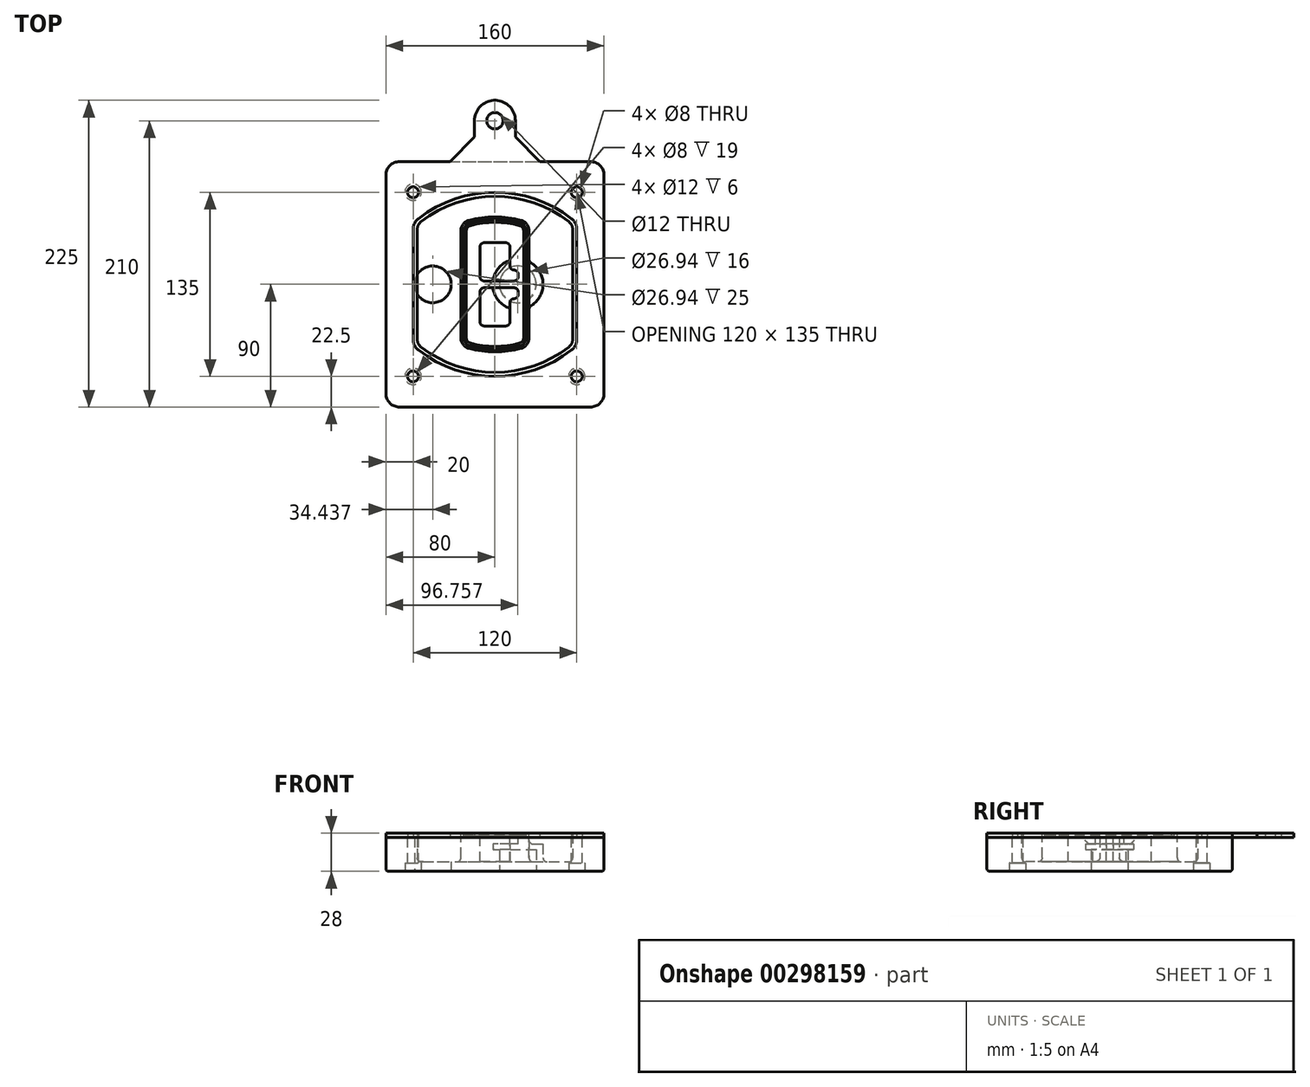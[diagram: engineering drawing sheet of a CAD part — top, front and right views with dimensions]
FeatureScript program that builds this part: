
annotation { "Feature Type Name" : "Feature", "Feature Type Description" : "" }
export const myFeature = defineFeature(function(context is Context, id is Id, definition is map)
    precondition{}
    {
        {
            var Q0;
            Q0=qCreatedBy(makeId("Top.planeOp"),FACE);
            var sketch = newSketch(context, id + "F0", { "sketchPlane" : qUnion([Q0])});
            skPoint(sketch, "E0.rect.middle", {"position": v(0, 0) * mm});
            skLineSegment(sketch, "E1.bottom", {"start": v(-70, -90) * mm, "end": v(70, -90) * mm});
            skLineSegment(sketch, "E1.top", {"start": v(-70, 90) * mm, "end": v(70, 90) * mm});
            skLineSegment(sketch, "E1.left", {"start": v(-80, -80) * mm, "end": v(-80, 80) * mm});
            skLineSegment(sketch, "E1.right", {"start": v(80, -80) * mm, "end": v(80, 80) * mm});
            skLineSegment(sketch, "E2", {"start": v(-80, 90) * mm, "end": v(80, -90) * mm, "construction": true});
            skLineSegment(sketch, "E3", {"start": v(80, 90) * mm, "end": v(-80, -90) * mm, "construction": true});
            skCircle(sketch, "E4", {"center": v(-60, 67.5) * mm, "radius": 4 * mm});
            skCircle(sketch, "E5", {"center": v(60, 67.5) * mm, "radius": 4 * mm});
            skCircle(sketch, "E6", {"center": v(60, -67.5) * mm, "radius": 4 * mm});
            skCircle(sketch, "E7", {"center": v(-60, -67.5) * mm, "radius": 4 * mm});
            skLineSegment(sketch, "E8", {"start": v(-60, 67.5) * mm, "end": v(60, 67.5) * mm, "construction": true});
            skLineSegment(sketch, "E9", {"start": v(60, 67.5) * mm, "end": v(60, -67.5) * mm, "construction": true});
            skLineSegment(sketch, "E10", {"start": v(60, -67.5) * mm, "end": v(-60, -67.5) * mm, "construction": true});
            skLineSegment(sketch, "E11", {"start": v(-60, -67.5) * mm, "end": v(-60, 67.5) * mm, "construction": true});
            skLineSegment(sketch, "E12", {"start": v(-60, 40.3) * mm, "end": v(-60, -40.3) * mm});
            skLineSegment(sketch, "E13", {"start": v(60, 40.3) * mm, "end": v(60, -40.3) * mm});
            skArc(sketch, "E14", {"start": v(56.15, 48.18) * mm, "mid": v(0, 67.5) * mm, "end": v(-56.15, 48.18) * mm});
            skArc(sketch, "E15", {"start": v(-56.15, -48.18) * mm, "mid": v(0, -67.5) * mm, "end": v(56.15, -48.18) * mm});
            skLineSegment(sketch, "E16", {"start": v(-60, 0) * mm, "end": v(60, 0) * mm, "construction": true});
            skPoint(sketch, "E17.visualSharp", {"position": v(-60, -45) * mm});
            skArc(sketch, "E17.filletArc", {"start": v(-60, -40.3) * mm, "mid": v(-58.99, -44.68) * mm, "end": v(-56.15, -48.18) * mm});
            skPoint(sketch, "E18.visualSharp", {"position": v(-60, 45) * mm});
            skArc(sketch, "E18.filletArc", {"start": v(-56.15, 48.18) * mm, "mid": v(-58.99, 44.68) * mm, "end": v(-60, 40.3) * mm});
            skPoint(sketch, "E19.visualSharp", {"position": v(60, 45) * mm});
            skArc(sketch, "E19.filletArc", {"start": v(60, 40.3) * mm, "mid": v(58.99, 44.68) * mm, "end": v(56.15, 48.18) * mm});
            skPoint(sketch, "E20.visualSharp", {"position": v(60, -45) * mm});
            skArc(sketch, "E20.filletArc", {"start": v(56.15, -48.18) * mm, "mid": v(58.99, -44.68) * mm, "end": v(60, -40.3) * mm});
            skPoint(sketch, "E21.visualSharp", {"position": v(-80, 90) * mm});
            skArc(sketch, "E21.filletArc", {"start": v(-70, 90) * mm, "mid": v(-77.07, 87.07) * mm, "end": v(-80, 80) * mm});
            skPoint(sketch, "E22.visualSharp", {"position": v(80, 90) * mm});
            skArc(sketch, "E22.filletArc", {"start": v(80, 80) * mm, "mid": v(77.07, 87.07) * mm, "end": v(70, 90) * mm});
            skPoint(sketch, "E23.visualSharp", {"position": v(80, -90) * mm});
            skArc(sketch, "E23.filletArc", {"start": v(70, -90) * mm, "mid": v(77.07, -87.07) * mm, "end": v(80, -80) * mm});
            skPoint(sketch, "E24.visualSharp", {"position": v(-80, -90) * mm});
            skArc(sketch, "E24.filletArc", {"start": v(-80, -80) * mm, "mid": v(-77.07, -87.07) * mm, "end": v(-70, -90) * mm});
            skArc(sketch, "E25.0", {"start": v(57, 40.3) * mm, "mid": v(56.3, 43.36) * mm, "end": v(54.3, 45.81) * mm});
            skLineSegment(sketch, "E25.1", {"start": v(57, 40.3) * mm, "end": v(57, -40.3) * mm});
            skArc(sketch, "E25.2", {"start": v(54.3, -45.81) * mm, "mid": v(56.3, -43.36) * mm, "end": v(57, -40.3) * mm});
            skArc(sketch, "E25.3", {"start": v(-54.3, -45.81) * mm, "mid": v(0, -64.5) * mm, "end": v(54.3, -45.81) * mm});
            skArc(sketch, "E25.4", {"start": v(-57, -40.3) * mm, "mid": v(-56.3, -43.36) * mm, "end": v(-54.3, -45.81) * mm});
            skArc(sketch, "E25.5", {"start": v(54.3, 45.81) * mm, "mid": v(0, 64.5) * mm, "end": v(-54.3, 45.81) * mm});
            skLineSegment(sketch, "E25.6", {"start": v(-57, 40.3) * mm, "end": v(-57, -40.3) * mm});
            skArc(sketch, "E25.7", {"start": v(-54.3, 45.81) * mm, "mid": v(-56.3, 43.36) * mm, "end": v(-57, 40.3) * mm});
            skArc(sketch, "E26.0", {"start": v(-58.62, 51.33) * mm, "mid": v(-62.58, 46.43) * mm, "end": v(-64, 40.3) * mm});
            skArc(sketch, "E26.1", {"start": v(58.62, 51.33) * mm, "mid": v(0, 71.5) * mm, "end": v(-58.62, 51.33) * mm});
            skArc(sketch, "E26.2", {"start": v(64, 40.3) * mm, "mid": v(62.58, 46.43) * mm, "end": v(58.62, 51.33) * mm});
            skLineSegment(sketch, "E26.3", {"start": v(64, 40.3) * mm, "end": v(64, -40.3) * mm});
            skArc(sketch, "E26.4", {"start": v(58.62, -51.33) * mm, "mid": v(62.58, -46.43) * mm, "end": v(64, -40.3) * mm});
            skLineSegment(sketch, "E26.5", {"start": v(-64, 40.3) * mm, "end": v(-64, -40.3) * mm});
            skArc(sketch, "E26.6", {"start": v(-58.62, -51.33) * mm, "mid": v(0, -71.5) * mm, "end": v(58.62, -51.33) * mm});
            skArc(sketch, "E26.7", {"start": v(-64, -40.3) * mm, "mid": v(-62.58, -46.43) * mm, "end": v(-58.62, -51.33) * mm});
            skSolve(sketch);
        }
        {
            var Q0;
            Q0=makeQuery(id+"F0.imprint","IMPRINT",FACE,{"disambiguationData":[TD([[makeQuery(id+"F0.imprint","IMPRINT",EDGE,{"derivedFrom":sQuery(id+"F0.wireOp",EDGE,"E1.bottom")}),1.0]])]});
            var Q1;
            Q1=makeQuery(id+"F0.imprint","IMPRINT",FACE,{"disambiguationData":[TD([[makeQuery(id+"F0.imprint","IMPRINT",EDGE,{"derivedFrom":sQuery(id+"F0.wireOp",EDGE,"E12")}),1.0]])]});
            var Q2;
            Q2=makeQuery(id+"F0.imprint","IMPRINT",FACE,{"disambiguationData":[TD([[makeQuery(id+"F0.imprint","IMPRINT",EDGE,{"derivedFrom":sQuery(id+"F0.wireOp",EDGE,"E25.0")}),1.0]])]});
            var Q3;
            Q3=makeQuery(id+"F0.imprint","IMPRINT",FACE,{"disambiguationData":[TD([[makeQuery(id+"F0.imprint","IMPRINT",EDGE,{"derivedFrom":sQuery(id+"F0.wireOp",EDGE,"E12")}),-1.0]])]});
            extrude(context, id + "F1", {"entities" : qUnion([Q0, Q1, Q2, Q3]), "oppositeDirection" : true, "depth" : 25 * mm});
        }
        {
            var Q0;
            Q0=makeQuery(id+"F0.imprint","IMPRINT",FACE,{"disambiguationData":[TD([[makeQuery(id+"F0.imprint","IMPRINT",EDGE,{"derivedFrom":sQuery(id+"F0.wireOp",EDGE,"E12")}),1.0]])]});
            extrude(context, id + "F2", {"entities" : qUnion([Q0]), "operationType" : NewBodyOperationType.ADD, "depth" : 3 * mm});
        }
        {
            var Q0;
            Q0=makeQuery(id+"F0.imprint","IMPRINT",FACE,{"disambiguationData":[TD([[makeQuery(id+"F0.imprint","IMPRINT",EDGE,{"derivedFrom":sQuery(id+"F0.wireOp",EDGE,"E25.0")}),1.0]])]});
            extrude(context, id + "F3", {"entities" : qUnion([Q0]), "operationType" : NewBodyOperationType.REMOVE, "oppositeDirection" : true, "depth" : 18 * mm});
        }
        {
            var Q0;
            Q0=makeQuery(id+"F2.opExtrude","CAP_FACE",FACE,{"disambiguationData":[OSD([sQuery(id+"F0.wireOp",EDGE,"E12"),sQuery(id+"F0.wireOp",EDGE,"E13"),sQuery(id+"F0.wireOp",EDGE,"E14"),sQuery(id+"F0.wireOp",EDGE,"E15"),sQuery(id+"F0.wireOp",EDGE,"E17.filletArc"),sQuery(id+"F0.wireOp",EDGE,"E18.filletArc"),sQuery(id+"F0.wireOp",EDGE,"E19.filletArc"),sQuery(id+"F0.wireOp",EDGE,"E20.filletArc"),sQuery(id+"F0.wireOp",EDGE,"E25.0"),sQuery(id+"F0.wireOp",EDGE,"E25.1"),sQuery(id+"F0.wireOp",EDGE,"E25.2"),sQuery(id+"F0.wireOp",EDGE,"E25.3"),sQuery(id+"F0.wireOp",EDGE,"E25.4"),sQuery(id+"F0.wireOp",EDGE,"E25.5"),sQuery(id+"F0.wireOp",EDGE,"E25.6"),sQuery(id+"F0.wireOp",EDGE,"E25.7")])],"isStart":false});
            var sketch = newSketch(context, id + "F4", { "sketchPlane" : qUnion([Q0])});
            skArc(sketch, "E27.0", {"start": v(-19.08, -46.97) * mm, "mid": v(0, -49.5) * mm, "end": v(19.08, -46.97) * mm});
            skArc(sketch, "E28.0", {"start": v(19.08, 46.97) * mm, "mid": v(0, 49.5) * mm, "end": v(-19.08, 46.97) * mm});
            skLineSegment(sketch, "E29", {"start": v(-25, 39.25) * mm, "end": v(-25, -39.25) * mm});
            skLineSegment(sketch, "E30", {"start": v(25, 39.25) * mm, "end": v(25, -39.25) * mm});
            skLineSegment(sketch, "E31", {"start": v(-25, 45.1) * mm, "end": v(25, 45.1) * mm, "construction": true});
            skLineSegment(sketch, "E32", {"start": v(-25, -45.1) * mm, "end": v(25, -45.1) * mm, "construction": true});
            skPoint(sketch, "E33.visualSharp", {"position": v(-25, 45.1) * mm});
            skArc(sketch, "E33.filletArc", {"start": v(-19.08, 46.97) * mm, "mid": v(-23.35, 44.11) * mm, "end": v(-25, 39.25) * mm});
            skPoint(sketch, "E34.visualSharp", {"position": v(25, 45.1) * mm});
            skArc(sketch, "E34.filletArc", {"start": v(25, 39.25) * mm, "mid": v(23.35, 44.11) * mm, "end": v(19.08, 46.97) * mm});
            skPoint(sketch, "E35.visualSharp", {"position": v(25, -45.1) * mm});
            skArc(sketch, "E35.filletArc", {"start": v(19.08, -46.97) * mm, "mid": v(23.35, -44.11) * mm, "end": v(25, -39.25) * mm});
            skPoint(sketch, "E36.visualSharp", {"position": v(-25, -45.1) * mm});
            skArc(sketch, "E36.filletArc", {"start": v(-25, -39.25) * mm, "mid": v(-23.35, -44.11) * mm, "end": v(-19.08, -46.97) * mm});
            skArc(sketch, "E37.0", {"start": v(54.3, 45.81) * mm, "mid": v(0, 64.5) * mm, "end": v(-54.3, 45.81) * mm});
            skArc(sketch, "E37.1", {"start": v(-54.3, 45.81) * mm, "mid": v(-56.3, 43.36) * mm, "end": v(-57, 40.3) * mm});
            skLineSegment(sketch, "E37.2", {"start": v(-57, 40.3) * mm, "end": v(-57, -40.3) * mm});
            skArc(sketch, "E37.3", {"start": v(-57, -40.3) * mm, "mid": v(-56.3, -43.36) * mm, "end": v(-54.3, -45.81) * mm});
            skArc(sketch, "E37.4", {"start": v(-54.3, -45.81) * mm, "mid": v(0, -64.5) * mm, "end": v(54.3, -45.81) * mm});
            skArc(sketch, "E37.5", {"start": v(54.3, -45.81) * mm, "mid": v(56.3, -43.36) * mm, "end": v(57, -40.3) * mm});
            skLineSegment(sketch, "E37.6", {"start": v(57, 40.3) * mm, "end": v(57, -40.3) * mm});
            skArc(sketch, "E37.7", {"start": v(57, 40.3) * mm, "mid": v(56.3, 43.36) * mm, "end": v(54.3, 45.81) * mm});
            skLineSegment(sketch, "E38.0", {"start": v(23, 39.25) * mm, "end": v(23, -39.25) * mm});
            skArc(sketch, "E38.1", {"start": v(18.56, -45.04) * mm, "mid": v(21.76, -42.9) * mm, "end": v(23, -39.25) * mm});
            skArc(sketch, "E38.2", {"start": v(-18.56, -45.04) * mm, "mid": v(0, -47.5) * mm, "end": v(18.56, -45.04) * mm});
            skArc(sketch, "E38.3", {"start": v(-23, -39.25) * mm, "mid": v(-21.76, -42.9) * mm, "end": v(-18.56, -45.04) * mm});
            skLineSegment(sketch, "E38.4", {"start": v(-23, 39.25) * mm, "end": v(-23, -39.25) * mm});
            skArc(sketch, "E38.5", {"start": v(23, 39.25) * mm, "mid": v(21.76, 42.9) * mm, "end": v(18.56, 45.04) * mm});
            skArc(sketch, "E38.6", {"start": v(-18.56, 45.04) * mm, "mid": v(-21.76, 42.9) * mm, "end": v(-23, 39.25) * mm});
            skArc(sketch, "E38.7", {"start": v(18.56, 45.04) * mm, "mid": v(0, 47.5) * mm, "end": v(-18.56, 45.04) * mm});
            skArc(sketch, "E39.0", {"start": v(21, 39.25) * mm, "mid": v(20.18, 41.68) * mm, "end": v(18.04, 43.1) * mm});
            skLineSegment(sketch, "E39.1", {"start": v(21, 39.25) * mm, "end": v(21, -39.25) * mm});
            skArc(sketch, "E39.2", {"start": v(18.04, -43.1) * mm, "mid": v(20.18, -41.68) * mm, "end": v(21, -39.25) * mm});
            skArc(sketch, "E39.3", {"start": v(-18.04, -43.1) * mm, "mid": v(0, -45.5) * mm, "end": v(18.04, -43.1) * mm});
            skArc(sketch, "E39.4", {"start": v(-21, -39.25) * mm, "mid": v(-20.18, -41.68) * mm, "end": v(-18.04, -43.1) * mm});
            skArc(sketch, "E39.5", {"start": v(18.04, 43.1) * mm, "mid": v(0, 45.5) * mm, "end": v(-18.04, 43.1) * mm});
            skLineSegment(sketch, "E39.6", {"start": v(-21, 39.25) * mm, "end": v(-21, -39.25) * mm});
            skArc(sketch, "E39.7", {"start": v(-18.04, 43.1) * mm, "mid": v(-20.18, 41.68) * mm, "end": v(-21, 39.25) * mm});
            skLineSegment(sketch, "E40", {"start": v(-25, 0) * mm, "end": v(25, 0) * mm, "construction": true});
            skLineSegment(sketch, "E41", {"start": v(-11, 5.5) * mm, "end": v(-11, 27.5) * mm});
            skLineSegment(sketch, "E42", {"start": v(-8, 30.5) * mm, "end": v(8, 30.5) * mm});
            skLineSegment(sketch, "E43", {"start": v(11, 27.5) * mm, "end": v(11, 13.5) * mm});
            skLineSegment(sketch, "E44", {"start": v(14, 10.5) * mm, "end": v(14, 10.5) * mm});
            skLineSegment(sketch, "E45", {"start": v(17, 7.5) * mm, "end": v(17, 5.5) * mm});
            skLineSegment(sketch, "E46", {"start": v(14, 2.5) * mm, "end": v(-8, 2.5) * mm});
            skPoint(sketch, "E47.visualSharp", {"position": v(-11, 30.5) * mm});
            skArc(sketch, "E47.filletArc", {"start": v(-8, 30.5) * mm, "mid": v(-10.12, 29.62) * mm, "end": v(-11, 27.5) * mm});
            skPoint(sketch, "E48.visualSharp", {"position": v(11, 30.5) * mm});
            skArc(sketch, "E48.filletArc", {"start": v(11, 27.5) * mm, "mid": v(10.12, 29.62) * mm, "end": v(8, 30.5) * mm});
            skPoint(sketch, "E49.visualSharp", {"position": v(11, 10.5) * mm});
            skArc(sketch, "E49.filletArc", {"start": v(11, 13.5) * mm, "mid": v(11.88, 11.38) * mm, "end": v(14, 10.5) * mm});
            skPoint(sketch, "E50.visualSharp", {"position": v(17, 10.5) * mm});
            skArc(sketch, "E50.filletArc", {"start": v(17, 7.5) * mm, "mid": v(16.12, 9.62) * mm, "end": v(14, 10.5) * mm});
            skPoint(sketch, "E51.visualSharp", {"position": v(17, 2.5) * mm});
            skArc(sketch, "E51.filletArc", {"start": v(14, 2.5) * mm, "mid": v(16.12, 3.38) * mm, "end": v(17, 5.5) * mm});
            skPoint(sketch, "E52.visualSharp", {"position": v(-11, 2.5) * mm});
            skArc(sketch, "E52.filletArc", {"start": v(-11, 5.5) * mm, "mid": v(-10.12, 3.38) * mm, "end": v(-8, 2.5) * mm});
            skLineSegment(sketch, "E53.0.MirrorCS", {"start": v(14, -2.5) * mm, "end": v(-8, -2.5) * mm});
            skArc(sketch, "E54.0.MirrorCS", {"start": v(-11, -5.5) * mm, "mid": v(-10.12, -3.38) * mm, "end": v(-8, -2.5) * mm});
            skLineSegment(sketch, "E55.0.MirrorCS", {"start": v(-11, -5.5) * mm, "end": v(-11, -27.5) * mm});
            skArc(sketch, "E56.0.MirrorCS", {"start": v(-8, -30.5) * mm, "mid": v(-10.12, -29.62) * mm, "end": v(-11, -27.5) * mm});
            skLineSegment(sketch, "E57.0.MirrorCS", {"start": v(-8, -30.5) * mm, "end": v(8, -30.5) * mm});
            skArc(sketch, "E58.0.MirrorCS", {"start": v(11, -27.5) * mm, "mid": v(10.12, -29.62) * mm, "end": v(8, -30.5) * mm});
            skLineSegment(sketch, "E59.0.MirrorCS", {"start": v(11, -27.5) * mm, "end": v(11, -13.5) * mm});
            skArc(sketch, "E60.0.MirrorCS", {"start": v(11, -13.5) * mm, "mid": v(11.88, -11.38) * mm, "end": v(14, -10.5) * mm});
            skArc(sketch, "E61.0.MirrorCS", {"start": v(17, -7.5) * mm, "mid": v(16.12, -9.62) * mm, "end": v(14, -10.5) * mm});
            skLineSegment(sketch, "E62.0.MirrorCS", {"start": v(17, -7.5) * mm, "end": v(17, -5.5) * mm});
            skArc(sketch, "E63.0.MirrorCS", {"start": v(14, -2.5) * mm, "mid": v(16.12, -3.38) * mm, "end": v(17, -5.5) * mm});
            skSolve(sketch);
        }
        {
            var Q0;
            Q0=makeQuery(id+"F4.imprint","IMPRINT",FACE,{"disambiguationData":[TD([[makeQuery(id+"F4.imprint","IMPRINT",EDGE,{"derivedFrom":sQuery(id+"F4.wireOp",EDGE,"E27.0")}),1.0]])]});
            var Q1;
            Q1=makeQuery(id+"F4.imprint","IMPRINT",FACE,{"disambiguationData":[TD([[makeQuery(id+"F4.imprint","IMPRINT",EDGE,{"derivedFrom":sQuery(id+"F4.wireOp",EDGE,"E38.0")}),-1.0]])]});
            var Q2;
            Q2=makeQuery(id+"F4.imprint","IMPRINT",FACE,{"disambiguationData":[TD([[makeQuery(id+"F4.imprint","IMPRINT",EDGE,{"derivedFrom":sQuery(id+"F4.wireOp",EDGE,"E39.0")}),1.0]])]});
            extrude(context, id + "F5", {"entities" : qUnion([Q0, Q1, Q2]), "operationType" : NewBodyOperationType.ADD, "endBound" : BoundingType.UP_TO_NEXT, "oppositeDirection" : true, "depth" : 25 * mm});
        }
        {
            var Q0;
            Q0=makeQuery(id+"F4.imprint","IMPRINT",FACE,{"disambiguationData":[TD([[makeQuery(id+"F4.imprint","IMPRINT",EDGE,{"derivedFrom":sQuery(id+"F4.wireOp",EDGE,"E38.0")}),-1.0]])]});
            extrude(context, id + "F6", {"entities" : qUnion([Q0]), "operationType" : NewBodyOperationType.REMOVE, "oppositeDirection" : true, "depth" : 2 * mm});
        }
        {
            var Q0;
            Q0=makeQuery(id+"F1.opExtrude","CAP_FACE",FACE,{"disambiguationData":[OSD([sQuery(id+"F0.wireOp",EDGE,"E1.bottom"),sQuery(id+"F0.wireOp",EDGE,"E1.top"),sQuery(id+"F0.wireOp",EDGE,"E1.left"),sQuery(id+"F0.wireOp",EDGE,"E1.right"),sQuery(id+"F0.wireOp",EDGE,"E4"),sQuery(id+"F0.wireOp",EDGE,"E5"),sQuery(id+"F0.wireOp",EDGE,"E6"),sQuery(id+"F0.wireOp",EDGE,"E7"),sQuery(id+"F0.wireOp",EDGE,"E21.filletArc"),sQuery(id+"F0.wireOp",EDGE,"E22.filletArc"),sQuery(id+"F0.wireOp",EDGE,"E23.filletArc"),sQuery(id+"F0.wireOp",EDGE,"E24.filletArc")])],"isStart":false});
            var sketch = newSketch(context, id + "F7", { "sketchPlane" : qUnion([Q0])});
            skCircle(sketch, "E64", {"center": v(16.76, 0) * mm, "radius": 13.47 * mm});
            skCircle(sketch, "E65", {"center": v(-45.56, 0) * mm, "radius": 13.47 * mm});
            skLineSegment(sketch, "E66", {"start": v(80, 0) * mm, "end": v(-80, 0) * mm});
            skCircle(sketch, "E67", {"center": v(16.76, 0) * mm, "radius": 18.47 * mm});
            skCircle(sketch, "E68", {"center": v(60, -67.5) * mm, "radius": 6 * mm});
            skCircle(sketch, "E69", {"center": v(-60, -67.5) * mm, "radius": 6 * mm});
            skCircle(sketch, "E70", {"center": v(-60, 67.5) * mm, "radius": 6 * mm});
            skCircle(sketch, "E71", {"center": v(60, 67.5) * mm, "radius": 6 * mm});
            skSolve(sketch);
        }
        {
            var Q0;
            {var subQ1=sQuery(id+"F7.wireOp",EDGE,"E66");var subQ4=sQuery(id+"F7.wireOp",EDGE,"E64");var subQ6=makeQuery(id+"F7.imprint","INTERSECT",VERTEX,{"disambiguationData":[OD(0.0)],"derivedFrom":[subQ4,subQ1]});Q0=makeQuery(id+"F7.imprint","IMPRINT",FACE,{"disambiguationData":[TD([[makeQuery(id+"F7.imprint","IMPRINT",EDGE,{"disambiguationData":[TD([[subQ6,-1.0]])],"derivedFrom":subQ4}),-1.0]])]});}
            var Q1;
            {var subQ0=sQuery(id+"F7.wireOp",EDGE,"E66");var subQ1=sQuery(id+"F7.wireOp",EDGE,"E64");var subQ3=makeQuery(id+"F7.imprint","INTERSECT",VERTEX,{"disambiguationData":[OD(0.0)],"derivedFrom":[subQ1,subQ0]});Q1=makeQuery(id+"F7.imprint","IMPRINT",FACE,{"disambiguationData":[TD([[makeQuery(id+"F7.imprint","IMPRINT",EDGE,{"disambiguationData":[TD([[subQ3,-1.0]])],"derivedFrom":subQ1}),1.0]])]});}
            var Q2;
            {var subQ0=sQuery(id+"F7.wireOp",EDGE,"E66");var subQ1=sQuery(id+"F7.wireOp",EDGE,"E64");var subQ3=makeQuery(id+"F7.imprint","INTERSECT",VERTEX,{"disambiguationData":[OD(0.0)],"derivedFrom":[subQ1,subQ0]});Q2=makeQuery(id+"F7.imprint","IMPRINT",FACE,{"disambiguationData":[TD([[makeQuery(id+"F7.imprint","IMPRINT",EDGE,{"disambiguationData":[TD([[subQ3,1.0]])],"derivedFrom":subQ1}),1.0]])]});}
            var Q3;
            {var subQ1=sQuery(id+"F7.wireOp",EDGE,"E66");var subQ4=sQuery(id+"F7.wireOp",EDGE,"E64");var subQ6=makeQuery(id+"F7.imprint","INTERSECT",VERTEX,{"disambiguationData":[OD(0.0)],"derivedFrom":[subQ4,subQ1]});Q3=makeQuery(id+"F7.imprint","IMPRINT",FACE,{"disambiguationData":[TD([[makeQuery(id+"F7.imprint","IMPRINT",EDGE,{"disambiguationData":[TD([[subQ6,1.0]])],"derivedFrom":subQ4}),-1.0]])]});}
            extrude(context, id + "F8", {"entities" : qUnion([Q0, Q1, Q2, Q3]), "operationType" : NewBodyOperationType.ADD, "oppositeDirection" : true, "depth" : 20 * mm});
        }
        {
            var Q0;
            {var subQ0=sQuery(id+"F7.wireOp",EDGE,"E66");var subQ1=sQuery(id+"F7.wireOp",EDGE,"E64");var subQ3=makeQuery(id+"F7.imprint","INTERSECT",VERTEX,{"disambiguationData":[OD(0.0)],"derivedFrom":[subQ1,subQ0]});Q0=makeQuery(id+"F7.imprint","IMPRINT",FACE,{"disambiguationData":[TD([[makeQuery(id+"F7.imprint","IMPRINT",EDGE,{"disambiguationData":[TD([[subQ3,-1.0]])],"derivedFrom":subQ1}),1.0]])]});}
            var Q1;
            {var subQ0=sQuery(id+"F7.wireOp",EDGE,"E66");var subQ1=sQuery(id+"F7.wireOp",EDGE,"E64");var subQ3=makeQuery(id+"F7.imprint","INTERSECT",VERTEX,{"disambiguationData":[OD(0.0)],"derivedFrom":[subQ1,subQ0]});Q1=makeQuery(id+"F7.imprint","IMPRINT",FACE,{"disambiguationData":[TD([[makeQuery(id+"F7.imprint","IMPRINT",EDGE,{"disambiguationData":[TD([[subQ3,1.0]])],"derivedFrom":subQ1}),1.0]])]});}
            extrude(context, id + "F9", {"entities" : qUnion([Q0, Q1]), "operationType" : NewBodyOperationType.REMOVE, "oppositeDirection" : true, "depth" : 16 * mm});
        }
        {
            var Q0;
            {var subQ0=sQuery(id+"F7.wireOp",EDGE,"E66");var subQ1=sQuery(id+"F7.wireOp",EDGE,"E65");var subQ3=makeQuery(id+"F7.imprint","INTERSECT",VERTEX,{"disambiguationData":[OD(0.0)],"derivedFrom":[subQ1,subQ0]});Q0=makeQuery(id+"F7.imprint","IMPRINT",FACE,{"disambiguationData":[TD([[makeQuery(id+"F7.imprint","IMPRINT",EDGE,{"disambiguationData":[TD([[subQ3,-1.0]])],"derivedFrom":subQ1}),1.0]])]});}
            var Q1;
            {var subQ0=sQuery(id+"F7.wireOp",EDGE,"E66");var subQ1=sQuery(id+"F7.wireOp",EDGE,"E65");var subQ3=makeQuery(id+"F7.imprint","INTERSECT",VERTEX,{"disambiguationData":[OD(0.0)],"derivedFrom":[subQ1,subQ0]});Q1=makeQuery(id+"F7.imprint","IMPRINT",FACE,{"disambiguationData":[TD([[makeQuery(id+"F7.imprint","IMPRINT",EDGE,{"disambiguationData":[TD([[subQ3,1.0]])],"derivedFrom":subQ1}),1.0]])]});}
            extrude(context, id + "F10", {"entities" : qUnion([Q0, Q1]), "operationType" : NewBodyOperationType.REMOVE, "oppositeDirection" : true, "depth" : 25 * mm});
        }
        {
            var Q0;
            Q0=makeQuery(id+"F7.imprint","IMPRINT",FACE,{"disambiguationData":[TD([[makeQuery(id+"F7.imprint","IMPRINT",EDGE,{"derivedFrom":sQuery(id+"F7.wireOp",EDGE,"E68")}),1.0]])]});
            var Q1;
            Q1=makeQuery(id+"F7.imprint","IMPRINT",FACE,{"disambiguationData":[TD([[makeQuery(id+"F7.imprint","IMPRINT",EDGE,{"derivedFrom":makeQuery(id+"F1.opExtrude","CAP_EDGE",EDGE,{"disambiguationData":[OSD([sQuery(id+"F0.wireOp",EDGE,"E5")])],"isStart":false})}),-1.0]])]});
            var Q2;
            Q2=makeQuery(id+"F7.imprint","IMPRINT",FACE,{"disambiguationData":[TD([[makeQuery(id+"F7.imprint","IMPRINT",EDGE,{"derivedFrom":sQuery(id+"F7.wireOp",EDGE,"E69")}),1.0]])]});
            var Q3;
            Q3=makeQuery(id+"F7.imprint","IMPRINT",FACE,{"disambiguationData":[TD([[makeQuery(id+"F7.imprint","IMPRINT",EDGE,{"derivedFrom":makeQuery(id+"F1.opExtrude","CAP_EDGE",EDGE,{"disambiguationData":[OSD([sQuery(id+"F0.wireOp",EDGE,"E4")])],"isStart":false})}),-1.0]])]});
            var Q4;
            Q4=makeQuery(id+"F7.imprint","IMPRINT",FACE,{"disambiguationData":[TD([[makeQuery(id+"F7.imprint","IMPRINT",EDGE,{"derivedFrom":sQuery(id+"F7.wireOp",EDGE,"E70")}),1.0]])]});
            var Q5;
            Q5=makeQuery(id+"F7.imprint","IMPRINT",FACE,{"disambiguationData":[TD([[makeQuery(id+"F7.imprint","IMPRINT",EDGE,{"derivedFrom":makeQuery(id+"F1.opExtrude","CAP_EDGE",EDGE,{"disambiguationData":[OSD([sQuery(id+"F0.wireOp",EDGE,"E7")])],"isStart":false})}),-1.0]])]});
            var Q6;
            Q6=makeQuery(id+"F7.imprint","IMPRINT",FACE,{"disambiguationData":[TD([[makeQuery(id+"F7.imprint","IMPRINT",EDGE,{"derivedFrom":sQuery(id+"F7.wireOp",EDGE,"E71")}),1.0]])]});
            var Q7;
            Q7=makeQuery(id+"F7.imprint","IMPRINT",FACE,{"disambiguationData":[TD([[makeQuery(id+"F7.imprint","IMPRINT",EDGE,{"derivedFrom":makeQuery(id+"F1.opExtrude","CAP_EDGE",EDGE,{"disambiguationData":[OSD([sQuery(id+"F0.wireOp",EDGE,"E6")])],"isStart":false})}),-1.0]])]});
            extrude(context, id + "F11", {"entities" : qUnion([Q0, Q1, Q2, Q3, Q4, Q5, Q6, Q7]), "operationType" : NewBodyOperationType.REMOVE, "oppositeDirection" : true, "depth" : 6 * mm});
        }
        {
            var Q0;
            Q0=makeQuery(id+"F9.boolean.opBoolean","COPY",FACE,{"derivedFrom":makeQuery(id+"F9.opExtrude","CAP_FACE",FACE,{"disambiguationData":[OSD([sQuery(id+"F7.wireOp",EDGE,"E64")])],"isStart":false})});
            var sketch = newSketch(context, id + "F12", { "sketchPlane" : qUnion([Q0])});
            skArc(sketch, "E72.0", {"start": v(11, 17.55) * mm, "mid": v(2.57, 11.82) * mm, "end": v(-1.54, 2.5) * mm});
            skArc(sketch, "E72.1", {"start": v(-1.54, -2.5) * mm, "mid": v(2.57, -11.82) * mm, "end": v(11, -17.55) * mm});
            skLineSegment(sketch, "E73", {"start": v(-1.54, -2.5) * mm, "end": v(14, -2.5) * mm});
            skLineSegment(sketch, "E74.0", {"start": v(14, 2.5) * mm, "end": v(-1.54, 2.5) * mm});
            skArc(sketch, "E74.1", {"start": v(14, 2.5) * mm, "mid": v(16.12, 3.38) * mm, "end": v(17, 5.5) * mm});
            skLineSegment(sketch, "E74.2", {"start": v(17, 7.5) * mm, "end": v(17, 5.5) * mm});
            skArc(sketch, "E74.3", {"start": v(17, 7.5) * mm, "mid": v(16.12, 9.62) * mm, "end": v(14, 10.5) * mm});
            skArc(sketch, "E74.4", {"start": v(11, 13.5) * mm, "mid": v(11.88, 11.38) * mm, "end": v(14, 10.5) * mm});
            skLineSegment(sketch, "E74.5", {"start": v(11, 17.55) * mm, "end": v(11, 13.5) * mm});
            skLineSegment(sketch, "E74.7", {"start": v(14, -2.5) * mm, "end": v(-1.54, -2.5) * mm});
            skArc(sketch, "E74.8", {"start": v(14, -2.5) * mm, "mid": v(16.12, -3.38) * mm, "end": v(17, -5.5) * mm});
            skLineSegment(sketch, "E74.9", {"start": v(17, -7.5) * mm, "end": v(17, -5.5) * mm});
            skArc(sketch, "E74.10", {"start": v(17, -7.5) * mm, "mid": v(16.12, -9.62) * mm, "end": v(14, -10.5) * mm});
            skArc(sketch, "E74.11", {"start": v(11, -13.5) * mm, "mid": v(11.88, -11.38) * mm, "end": v(14, -10.5) * mm});
            skLineSegment(sketch, "E74.12", {"start": v(11, -17.55) * mm, "end": v(11, -13.5) * mm});
            skPoint(sketch, "E75.orphan", {"position": v(11, -27.5) * mm});
            skPoint(sketch, "E76.orphan", {"position": v(-8, -2.5) * mm});
            skPoint(sketch, "E77.orphan", {"position": v(-8, 2.5) * mm});
            skPoint(sketch, "E78.orphan", {"position": v(11, 27.5) * mm});
            skSolve(sketch);
        }
        {
            var Q0;
            {var subQ7=sQuery(id+"F12.wireOp",EDGE,"E72.0");var subQ14=sQuery(id+"F12.wireOp",EDGE,"E72.1");var subQ16=sQuery(id+"F12.wireOp",EDGE,"E74.1");var subQ18=sQuery(id+"F12.wireOp",EDGE,"E74.8");Q0=qUnion([makeQuery(id+"F12.imprint","IMPRINT",FACE,{"disambiguationData":[TD([[makeQuery(id+"F12.imprint","IMPRINT",EDGE,{"derivedFrom":subQ7}),1.0]])]}),makeQuery(id+"F12.imprint","IMPRINT",FACE,{"disambiguationData":[TD([[makeQuery(id+"F12.imprint","IMPRINT",EDGE,{"derivedFrom":subQ14}),1.0]])]}),makeQuery(id+"F12.imprint","IMPRINT",FACE,{"disambiguationData":[TD([[makeQuery(id+"F12.imprint","IMPRINT",EDGE,{"derivedFrom":subQ16}),1.0]])]}),makeQuery(id+"F12.imprint","IMPRINT",FACE,{"disambiguationData":[TD([[makeQuery(id+"F12.imprint","IMPRINT",EDGE,{"derivedFrom":subQ18}),-1.0]])]})]);}
            var Q1;
            Q1=makeQuery(id+"F5.boolean.opBoolean","SPLIT",FACE,{"disambiguationData":[TD([makeQuery(id+"F5.opExtrude","SWEPT_FACE",FACE,{"disambiguationData":[OSD([sQuery(id+"F4.wireOp",EDGE,"E41")])]})])],"derivedFrom":makeQuery(id+"F3.boolean.opBoolean","COPY",FACE,{"derivedFrom":makeQuery(id+"F3.opExtrude","CAP_FACE",FACE,{"disambiguationData":[OSD([sQuery(id+"F0.wireOp",EDGE,"E25.0"),sQuery(id+"F0.wireOp",EDGE,"E25.1"),sQuery(id+"F0.wireOp",EDGE,"E25.2"),sQuery(id+"F0.wireOp",EDGE,"E25.3"),sQuery(id+"F0.wireOp",EDGE,"E25.4"),sQuery(id+"F0.wireOp",EDGE,"E25.5"),sQuery(id+"F0.wireOp",EDGE,"E25.6"),sQuery(id+"F0.wireOp",EDGE,"E25.7")])],"isStart":false})})});
            extrude(context, id + "F13", {"entities" : qUnion([Q0]), "operationType" : NewBodyOperationType.REMOVE, "endBound" : BoundingType.UP_TO_SURFACE, "endBoundEntityFace" : qUnion([Q1]), "depth" : 25 * mm});
        }
        {
            var Q0;
            Q0=makeQuery(id+"F3.boolean.opBoolean","COPY",EDGE,{"derivedFrom":makeQuery(id+"F3.opExtrude","CAP_EDGE",EDGE,{"disambiguationData":[OSD([sQuery(id+"F0.wireOp",EDGE,"E25.6")])],"isStart":false})});
            var Q1;
            Q1=makeQuery(id+"F8.boolean.opBoolean","INTERSECT",EDGE,{"derivedFrom":[makeQuery(id+"F5.opExtrude","SWEPT_FACE",FACE,{"disambiguationData":[OSD([sQuery(id+"F4.wireOp",EDGE,"E30")])]}),makeQuery(id+"F8.opExtrude","CAP_FACE",FACE,{"disambiguationData":[OSD([sQuery(id+"F7.wireOp",EDGE,"E67")])],"isStart":false})]});
            var Q2;
            Q2=makeQuery(id+"F8.boolean.opBoolean","INTERSECT",EDGE,{"disambiguationData":[OD(1.0)],"derivedFrom":[makeQuery(id+"F5.opExtrude","SWEPT_FACE",FACE,{"disambiguationData":[OSD([sQuery(id+"F4.wireOp",EDGE,"E30")])]}),makeQuery(id+"F8.opExtrude","SWEPT_FACE",FACE,{"disambiguationData":[OSD([sQuery(id+"F7.wireOp",EDGE,"E67")])]})]});
            var Q3;
            {var subQ0=sQuery(id+"F4.wireOp",EDGE,"E30");Q3=makeQuery(id+"F8.boolean.opBoolean","SPLIT",EDGE,{"disambiguationData":[TD([makeQuery(id+"F5.opExtrude","SWEPT_FACE",FACE,{"disambiguationData":[OSD([sQuery(id+"F4.wireOp",EDGE,"E35.filletArc")])]})])],"derivedFrom":makeQuery(id+"F5.opExtrude","CAP_EDGE",EDGE,{"disambiguationData":[OSD([subQ0])],"isStart":false})});}
            var Q4;
            {var subQ0=sQuery(id+"F0.wireOp",EDGE,"E25.7");var subQ1=sQuery(id+"F0.wireOp",EDGE,"E25.1");var subQ2=sQuery(id+"F0.wireOp",EDGE,"E25.6");var subQ3=sQuery(id+"F0.wireOp",EDGE,"E25.5");var subQ4=sQuery(id+"F0.wireOp",EDGE,"E25.4");var subQ5=sQuery(id+"F0.wireOp",EDGE,"E25.0");var subQ6=sQuery(id+"F0.wireOp",EDGE,"E25.2");var subQ7=sQuery(id+"F0.wireOp",EDGE,"E25.3");Q4=makeQuery(id+"F8.boolean.opBoolean","INTERSECT",EDGE,{"derivedFrom":[makeQuery(id+"F5.boolean.opBoolean","SPLIT",FACE,{"disambiguationData":[TD([makeQuery(id+"F2.opExtrude","SWEPT_FACE",FACE,{"disambiguationData":[OSD([subQ5])]})])],"derivedFrom":makeQuery(id+"F3.boolean.opBoolean","COPY",FACE,{"derivedFrom":makeQuery(id+"F3.opExtrude","CAP_FACE",FACE,{"disambiguationData":[OSD([subQ5,subQ1,subQ6,subQ7,subQ4,subQ3,subQ2,subQ0])],"isStart":false})})}),makeQuery(id+"F8.opExtrude","SWEPT_FACE",FACE,{"disambiguationData":[OSD([sQuery(id+"F7.wireOp",EDGE,"E67")])]})]});}
            var Q5;
            Q5=makeQuery(id+"F8.boolean.opBoolean","INTERSECT",EDGE,{"disambiguationData":[OD(0.0)],"derivedFrom":[makeQuery(id+"F5.opExtrude","SWEPT_FACE",FACE,{"disambiguationData":[OSD([sQuery(id+"F4.wireOp",EDGE,"E30")])]}),makeQuery(id+"F8.opExtrude","SWEPT_FACE",FACE,{"disambiguationData":[OSD([sQuery(id+"F7.wireOp",EDGE,"E67")])]})]});
            fillet(context, id + "F14", {"entities" : qUnion([Q0, Q1, Q2, Q3, Q4, Q5]), "radius" : 3 * mm, "tangentPropagation" : true, "allowEdgeOverflow" : false});
        }
        {
            var Q0;
            Q0=makeQuery(id+"F1.opExtrude","CAP_EDGE",EDGE,{"disambiguationData":[OSD([sQuery(id+"F0.wireOp",EDGE,"E1.bottom")])],"isStart":false});
            fillet(context, id + "F15", {"entities" : qUnion([Q0]), "radius" : 2 * mm, "tangentPropagation" : true, "allowEdgeOverflow" : false});
        }
        {
            var Q0;
            {var subQ0=sQuery(id+"F0.wireOp",EDGE,"E21.filletArc");var subQ1=sQuery(id+"F0.wireOp",EDGE,"E7");var subQ2=sQuery(id+"F0.wireOp",EDGE,"E6");var subQ3=sQuery(id+"F0.wireOp",EDGE,"E5");var subQ4=sQuery(id+"F0.wireOp",EDGE,"E4");var subQ5=sQuery(id+"F0.wireOp",EDGE,"E22.filletArc");var subQ6=sQuery(id+"F0.wireOp",EDGE,"E1.bottom");var subQ7=sQuery(id+"F0.wireOp",EDGE,"E1.right");var subQ8=sQuery(id+"F0.wireOp",EDGE,"E1.top");var subQ9=sQuery(id+"F0.wireOp",EDGE,"E1.left");var subQ10=sQuery(id+"F0.wireOp",EDGE,"E23.filletArc");var subQ11=sQuery(id+"F0.wireOp",EDGE,"E24.filletArc");Q0=makeQuery(id+"F2.boolean.opBoolean","SPLIT",FACE,{"disambiguationData":[TD([makeQuery(id+"F1.opExtrude","SWEPT_FACE",FACE,{"disambiguationData":[OSD([subQ6])]})])],"derivedFrom":makeQuery(id+"F1.opExtrude","CAP_FACE",FACE,{"disambiguationData":[OSD([subQ6,subQ8,subQ9,subQ7,subQ4,subQ3,subQ2,subQ1,subQ0,subQ5,subQ10,subQ11])],"isStart":true})});}
            var sketch = newSketch(context, id + "F16", { "sketchPlane" : qUnion([Q0])});
            skLineSegment(sketch, "E79", {"start": v(0, 90) * mm, "end": v(0, 120) * mm, "construction": true});
            skCircle(sketch, "E80", {"center": v(0, 120) * mm, "radius": 6 * mm});
            skArc(sketch, "E81", {"start": v(15, 120) * mm, "mid": v(0.68, 134.98) * mm, "end": v(-14.94, 121.36) * mm});
            skLineSegment(sketch, "E82", {"start": v(-14.94, 121.36) * mm, "end": v(-14.94, 108) * mm});
            skLineSegment(sketch, "E83", {"start": v(15, 120) * mm, "end": v(15, 108) * mm});
            skLineSegment(sketch, "E84", {"start": v(-14.94, 108) * mm, "end": v(-32.94, 90) * mm});
            skLineSegment(sketch, "E85", {"start": v(15, 108) * mm, "end": v(33, 90) * mm});
            skLineSegment(sketch, "E86", {"start": v(-80, 0) * mm, "end": v(80, 0) * mm, "construction": true});
            skArc(sketch, "E87.MirrorCS", {"start": v(15, -120) * mm, "mid": v(0.68, -134.98) * mm, "end": v(-14.94, -121.36) * mm});
            skCircle(sketch, "E88.MirrorC", {"center": v(0, -120) * mm, "radius": 6 * mm});
            skLineSegment(sketch, "E89.MirrorCS", {"start": v(15, -120) * mm, "end": v(15, -108) * mm});
            skLineSegment(sketch, "E90.MirrorCS", {"start": v(-14.94, -121.36) * mm, "end": v(-14.94, -108) * mm});
            skLineSegment(sketch, "E91.MirrorCS", {"start": v(0, -90) * mm, "end": v(0, -120) * mm, "construction": true});
            skLineSegment(sketch, "E92.MirrorCS", {"start": v(-14.94, -108) * mm, "end": v(-32.94, -90) * mm});
            skLineSegment(sketch, "E93.MirrorCS", {"start": v(15, -108) * mm, "end": v(33, -90) * mm});
            skSolve(sketch);
        }
        {
            var Q0;
            Q0=makeQuery(id+"F16.imprint","IMPRINT",FACE,{"disambiguationData":[TD([[makeQuery(id+"F16.imprint","IMPRINT",EDGE,{"derivedFrom":makeQuery(id+"F1.opExtrude","CAP_EDGE",EDGE,{"disambiguationData":[OSD([sQuery(id+"F0.wireOp",EDGE,"E1.left")])],"isStart":true})}),-1.0]])]});
            var Q1;
            Q1=makeQuery(id+"F16.imprint","IMPRINT",FACE,{"disambiguationData":[TD([[makeQuery(id+"F16.imprint","IMPRINT",EDGE,{"derivedFrom":sQuery(id+"F16.wireOp",EDGE,"E87.MirrorCS")}),-1.0]])]});
            var Q2;
            Q2=makeQuery(id+"F16.imprint","IMPRINT",FACE,{"disambiguationData":[TD([[makeQuery(id+"F16.imprint","IMPRINT",EDGE,{"derivedFrom":sQuery(id+"F16.wireOp",EDGE,"E80")}),-1.0]])]});
            var Q3;
            Q3=makeQuery(id+"F2.opExtrude","CAP_FACE",FACE,{"disambiguationData":[OSD([sQuery(id+"F0.wireOp",EDGE,"E12"),sQuery(id+"F0.wireOp",EDGE,"E13"),sQuery(id+"F0.wireOp",EDGE,"E14"),sQuery(id+"F0.wireOp",EDGE,"E15"),sQuery(id+"F0.wireOp",EDGE,"E17.filletArc"),sQuery(id+"F0.wireOp",EDGE,"E18.filletArc"),sQuery(id+"F0.wireOp",EDGE,"E19.filletArc"),sQuery(id+"F0.wireOp",EDGE,"E20.filletArc"),sQuery(id+"F0.wireOp",EDGE,"E25.0"),sQuery(id+"F0.wireOp",EDGE,"E25.1"),sQuery(id+"F0.wireOp",EDGE,"E25.2"),sQuery(id+"F0.wireOp",EDGE,"E25.3"),sQuery(id+"F0.wireOp",EDGE,"E25.4"),sQuery(id+"F0.wireOp",EDGE,"E25.5"),sQuery(id+"F0.wireOp",EDGE,"E25.6"),sQuery(id+"F0.wireOp",EDGE,"E25.7")])],"isStart":false});
            extrude(context, id + "F17", {"entities" : qUnion([Q0, Q1, Q2]), "endBound" : BoundingType.UP_TO_SURFACE, "endBoundEntityFace" : qUnion([Q3]), "depth" : 25 * mm});
        }
    });
